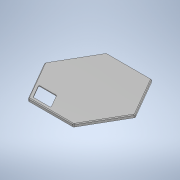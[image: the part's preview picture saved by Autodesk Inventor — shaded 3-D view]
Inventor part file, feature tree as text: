
AUTODESK INVENTOR PART (.ipt)
format: ipt  version: 2021 (Build 250183000, 183)  size: 173,568 bytes
history: native  units: mm
features: extrude x2, sketch x1, fillet x1, chamfer x1
ambient origin geometry x8: Origin, YZ Plane, XZ Plane, XY Plane, X Axis, Y Axis, Z Axis, Center Point
bodies: Solid1 (feature_tree)
feature tree (5):
  sketch  "Sketch1"  dims[d0=102.0mm d1=3.2mm d2=0.2mm d3=1.0mm d4=1.0mm d5=101.0mm d6=19.0mm d7=21.5mm d8=1.0mm d9=0.0mm d10=2.8mm d11=0.0mm d12=2.0mm d13=1.0mm d16=2.0mm d17=20.15mm d18=23.2mm d19=1.15mm d20=1.2mm d21=1.0mm d22=2.0mm d23=45.0deg]
  extrude  "Extrusion1"  Depth=2.0mm
  extrude  "Extrusion2"  Depth=2.0mm
  fillet  "Fillet1"  Radius=1.0mm
  chamfer  "Chamfer1"  Distance=1.0mm
